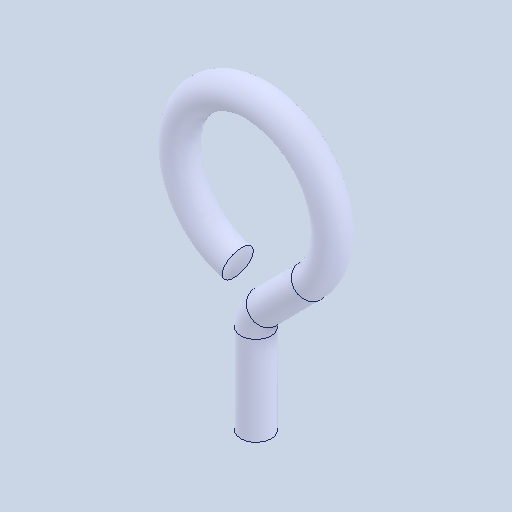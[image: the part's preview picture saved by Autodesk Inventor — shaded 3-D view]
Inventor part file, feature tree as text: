
AUTODESK INVENTOR PART (.ipt)
format: ipt  version: 2024.1 (Build 281209000, 209)  size: 127,488 bytes
history: native  units: in
note: dims shown in document units (in); Inventor stores cm internally (conversion verified against a paired STEP export)
features: sweep x1
ambient origin geometry x8: Origin, YZ Plane, XZ Plane, XY Plane, X Axis, Y Axis, Z Axis, Center Point
bodies: Solid1 (feature_tree)
feature tree (1):
  sweep  "Sweep1"
